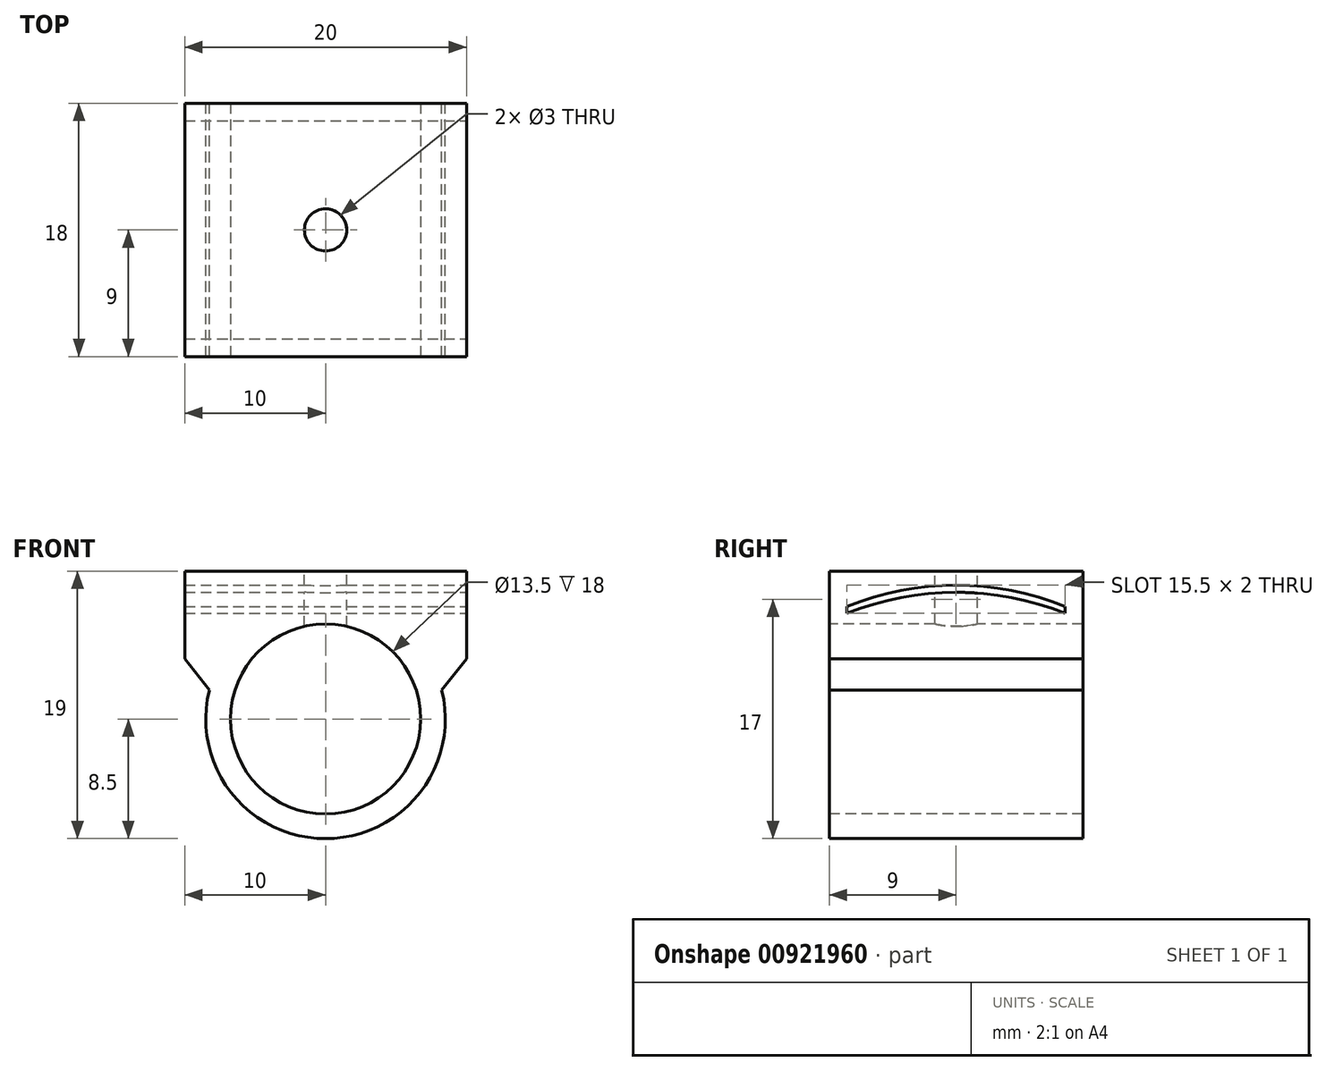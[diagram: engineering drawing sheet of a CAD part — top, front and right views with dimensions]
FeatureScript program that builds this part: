
annotation { "Feature Type Name" : "Feature", "Feature Type Description" : "" }
export const myFeature = defineFeature(function(context is Context, id is Id, definition is map)
    precondition{}
    {
        {
            var Q0;
            Q0=qCreatedBy(makeId("Front.planeOp"),FACE);
            var sketch = newSketch(context, id + "F0", { "sketchPlane" : qUnion([Q0])});
            skCircle(sketch, "E0", {"center": v(0, 0) * mm, "radius": 8.5 * mm});
            skSolve(sketch);
        }
        {
            var Q0;
            Q0 = qSketchRegion(id + "F0", true);
            extrude(context, id + "F1", {"entities" : qUnion([Q0]), "depth" : 18 * mm, "offsetDistance" : 25 * mm});
        }
        {
            var Q0;
            Q0=makeQuery(id+"F1.opExtrude","CAP_FACE",FACE,{"disambiguationData":[OSD([sQuery(id+"F0.wireOp",EDGE,"E0")])],"isStart":false});
            var sketch = newSketch(context, id + "F2", { "sketchPlane" : qUnion([Q0])});
            skCircle(sketch, "E1", {"center": v(0, 0) * mm, "radius": 6.75 * mm});
            skSolve(sketch);
        }
        {
            var Q0;
            Q0 = qSketchRegion(id + "F2", true);
            extrude(context, id + "F3", {"entities" : qUnion([Q0]), "operationType" : NewBodyOperationType.REMOVE, "endBound" : BoundingType.UP_TO_NEXT, "oppositeDirection" : true, "depth" : 25 * mm, "offsetDistance" : 25 * mm});
        }
        {
            var Q0;
            Q0=qCreatedBy(makeId("Right.planeOp"),FACE);
            var sketch = newSketch(context, id + "F4", { "sketchPlane" : qUnion([Q0])});
            skLineSegment(sketch, "E2.bottom", {"start": v(-18, 10.5) * mm, "end": v(0, 10.5) * mm});
            skLineSegment(sketch, "E2.top", {"start": v(-18, 7) * mm, "end": v(0, 7) * mm});
            skLineSegment(sketch, "E2.left", {"start": v(-18, 10.5) * mm, "end": v(-18, 7) * mm});
            skLineSegment(sketch, "E2.right", {"start": v(0, 10.5) * mm, "end": v(0, 7) * mm});
            skSolve(sketch);
        }
        {
            var Q0;
            Q0 = qSketchRegion(id + "F4", true);
            extrude(context, id + "F5", {"entities" : qUnion([Q0]), "operationType" : NewBodyOperationType.ADD, "endBound" : BoundingType.SYMMETRIC, "depth" : 20 * mm, "offsetDistance" : 25 * mm});
        }
        {
            var Q0;
            Q0=makeQuery(id+"F5.opExtrude","CAP_FACE",FACE,{"disambiguationData":[OSD([sQuery(id+"F4.wireOp",EDGE,"E2.bottom"),sQuery(id+"F4.wireOp",EDGE,"E2.top"),sQuery(id+"F4.wireOp",EDGE,"E2.left"),sQuery(id+"F4.wireOp",EDGE,"E2.right")])],"isStart":false});
            var sketch = newSketch(context, id + "F6", { "sketchPlane" : qUnion([Q0])});
            skLineSegment(sketch, "E3.left", {"start": v(-16.75, 7.5) * mm, "end": v(-16.75, 8) * mm});
            skLineSegment(sketch, "E3.right", {"start": v(-1.25, 7.5) * mm, "end": v(-1.25, 8) * mm});
            skArc(sketch, "E4", {"start": v(-1.25, 7.5) * mm, "mid": v(-9, 9) * mm, "end": v(-16.75, 7.5) * mm});
            skArc(sketch, "E5", {"start": v(-1.25, 8) * mm, "mid": v(-9, 9.5) * mm, "end": v(-16.75, 8) * mm});
            skPoint(sketch, "E6.orphan", {"position": v(-16.75, 9.5) * mm});
            skPoint(sketch, "E3.top.start.orphan", {"position": v(-9, 9.5) * mm});
            skPoint(sketch, "E7.orphan", {"position": v(-1.25, 9.5) * mm});
            skSolve(sketch);
        }
        {
            var Q0;
            Q0 = qSketchRegion(id + "F6", true);
            extrude(context, id + "F7", {"entities" : qUnion([Q0]), "operationType" : NewBodyOperationType.REMOVE, "endBound" : BoundingType.UP_TO_NEXT, "oppositeDirection" : true, "depth" : 25 * mm, "offsetDistance" : 25 * mm});
        }
        {
            var Q0;
            Q0=makeQuery(id+"F5.opExtrude","SWEPT_FACE",FACE,{"disambiguationData":[OSD([sQuery(id+"F4.wireOp",EDGE,"E2.bottom")])]});
            var sketch = newSketch(context, id + "F8", { "sketchPlane" : qUnion([Q0])});
            skCircle(sketch, "E8", {"center": v(0, -9) * mm, "radius": 1.5 * mm});
            skPoint(sketch, "E8.centerSnap0", {"position": v(-10, -9) * mm});
            skSolve(sketch);
        }
        {
            var Q0;
            Q0 = qSketchRegion(id + "F8", true);
            extrude(context, id + "F9", {"entities" : qUnion([Q0]), "operationType" : NewBodyOperationType.REMOVE, "oppositeDirection" : true, "depth" : 5 * mm, "offsetDistance" : 25 * mm});
        }
        {
            var Q0;
            Q0=makeQuery(id+"F5.boolean.opBoolean","INTERSECT",EDGE,{"disambiguationData":[OD(1.0)],"derivedFrom":[makeQuery(id+"F1.opExtrude","SWEPT_FACE",FACE,{"disambiguationData":[OSD([sQuery(id+"F0.wireOp",EDGE,"E0")])]}),makeQuery(id+"F5.opExtrude","SWEPT_FACE",FACE,{"disambiguationData":[OSD([sQuery(id+"F4.wireOp",EDGE,"E2.top")])]})]});
            var Q1;
            Q1=makeQuery(id+"F5.boolean.opBoolean","INTERSECT",EDGE,{"disambiguationData":[OD(0.0)],"derivedFrom":[makeQuery(id+"F1.opExtrude","SWEPT_FACE",FACE,{"disambiguationData":[OSD([sQuery(id+"F0.wireOp",EDGE,"E0")])]}),makeQuery(id+"F5.opExtrude","SWEPT_FACE",FACE,{"disambiguationData":[OSD([sQuery(id+"F4.wireOp",EDGE,"E2.top")])]})]});
            chamfer(context, id + "F10", {"entities" : qUnion([Q0, Q1]), "width" : 4 * mm, "tangentPropagation" : true});
        }
    });
